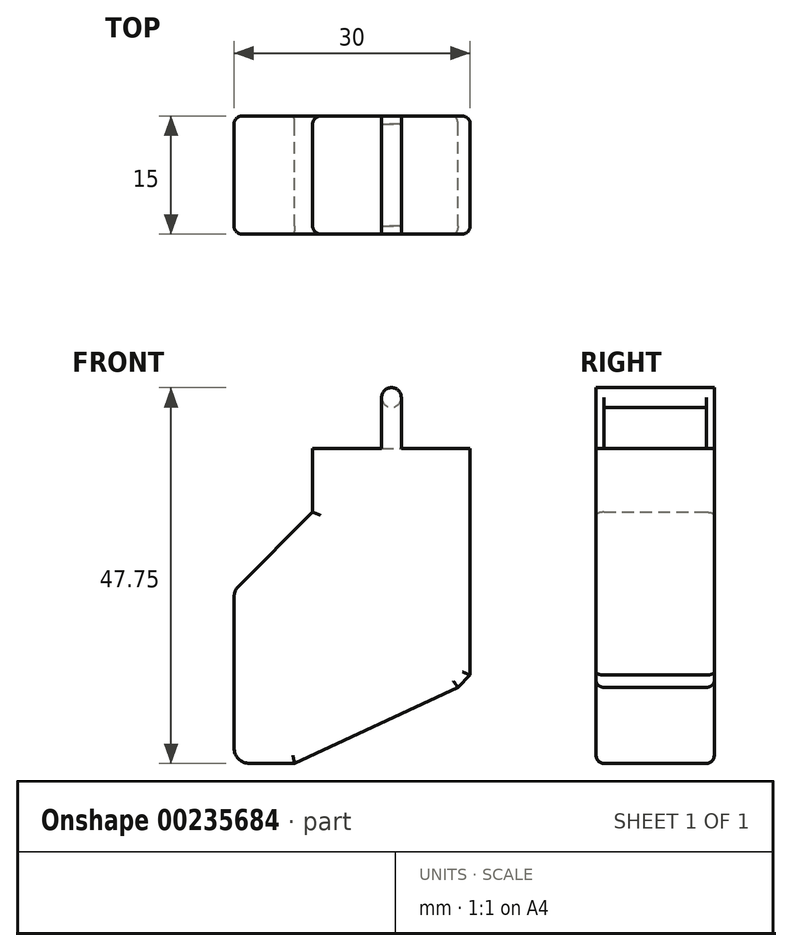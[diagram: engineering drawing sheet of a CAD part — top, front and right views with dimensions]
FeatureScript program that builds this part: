
annotation { "Feature Type Name" : "Feature", "Feature Type Description" : "" }
export const myFeature = defineFeature(function(context is Context, id is Id, definition is map)
    precondition{}
    {
        {
            var Q0;
            Q0=qCreatedBy(makeId("Front.planeOp"),FACE);
            var sketch = newSketch(context, id + "F0", { "sketchPlane" : qUnion([Q0])});
            skLineSegment(sketch, "E0", {"start": v(-8.09, 1.04) * mm, "end": v(-8.09, 15.54) * mm, "construction": true});
            skLineSegment(sketch, "E1", {"start": v(-8.09, 15.54) * mm, "end": v(-5.09, 15.54) * mm, "construction": true});
            skLineSegment(sketch, "E2", {"start": v(-5.09, 15.54) * mm, "end": v(-5.09, 1.04) * mm, "construction": true});
            skLineSegment(sketch, "E3", {"start": v(-5.09, 1.04) * mm, "end": v(-8.09, 1.04) * mm, "construction": true});
            skSolve(sketch);
        }
        {
            var Q0;
            Q0=qCreatedBy(makeId("Front.planeOp"),FACE);
            var sketch = newSketch(context, id + "F1", { "sketchPlane" : qUnion([Q0])});
            skPoint(sketch, "E4.1.end.orphan", {"position": v(-5.09, 15.54) * mm});
            skPoint(sketch, "E4.1.start.orphan", {"position": v(-8.09, 15.54) * mm});
            skPoint(sketch, "E5.end.orphan", {"position": v(-5.09, 1.04) * mm});
            skLineSegment(sketch, "E6", {"start": v(0, 12.27) * mm, "end": v(0, -9.67) * mm});
            skLineSegment(sketch, "E7", {"start": v(0, -9.67) * mm, "end": v(7.7, -9.67) * mm});
            skLineSegment(sketch, "E8", {"start": v(30, 1.56) * mm, "end": v(28.44, 0) * mm});
            skLineSegment(sketch, "E9", {"start": v(28.44, 0) * mm, "end": v(7.7, -9.67) * mm});
            skLineSegment(sketch, "E10", {"start": v(30, 1.56) * mm, "end": v(30, 30.33) * mm});
            skLineSegment(sketch, "E11", {"start": v(30, 30.33) * mm, "end": v(10, 30.33) * mm});
            skLineSegment(sketch, "E12", {"start": v(10, 30.33) * mm, "end": v(10, 22.27) * mm});
            skLineSegment(sketch, "E13", {"start": v(0, 12.27) * mm, "end": v(10, 22.27) * mm});
            skSolve(sketch);
        }
        {
            var Q0;
            Q0 = qSketchRegion(id + "F1", true);
            extrude(context, id + "F2", {"entities" : qUnion([Q0]), "depth" : 15 * mm});
        }
        {
            var Q0;
            Q0=makeQuery(id+"F2.opExtrude","SWEPT_EDGE",EDGE,{"disambiguationData":[OSD([sQuery(id+"F1.wireOp",EDGE,"lijkwqT2-R6P2-cXsj-bacL-RCKowQKFpfPk"),sQuery(id+"F1.wireOp",EDGE,"E6")])]});
            fillet(context, id + "F3", {"entities" : qUnion([Q0]), "radius" : 2 * mm, "tangentPropagation" : true, "allowEdgeOverflow" : false});
        }
        {
            var Q0;
            Q0=makeQuery(id+"F2.opExtrude","CAP_EDGE",EDGE,{"disambiguationData":[OSD([sQuery(id+"F1.wireOp",EDGE,"E13")])],"isStart":false});
            var Q1;
            Q1=makeQuery(id+"F2.opExtrude","CAP_EDGE",EDGE,{"disambiguationData":[OSD([sQuery(id+"F1.wireOp",EDGE,"E12")])],"isStart":false});
            var Q2;
            Q2=makeQuery(id+"F2.opExtrude","CAP_EDGE",EDGE,{"disambiguationData":[OSD([sQuery(id+"F1.wireOp",EDGE,"E12")])],"isStart":true});
            var Q3;
            Q3=makeQuery(id+"F2.opExtrude","CAP_EDGE",EDGE,{"disambiguationData":[OSD([sQuery(id+"F1.wireOp",EDGE,"E13")])],"isStart":true});
            var Q4;
            Q4=makeQuery(id+"F2.opExtrude","CAP_EDGE",EDGE,{"disambiguationData":[OSD([sQuery(id+"F1.wireOp",EDGE,"E9")])],"isStart":false});
            var Q5;
            Q5=makeQuery(id+"F2.opExtrude","CAP_EDGE",EDGE,{"disambiguationData":[OSD([sQuery(id+"F1.wireOp",EDGE,"E10")])],"isStart":false});
            var Q6;
            Q6=makeQuery(id+"F2.opExtrude","CAP_EDGE",EDGE,{"disambiguationData":[OSD([sQuery(id+"F1.wireOp",EDGE,"E8")])],"isStart":false});
            var Q7;
            Q7=makeQuery(id+"F2.opExtrude","CAP_EDGE",EDGE,{"disambiguationData":[OSD([sQuery(id+"F1.wireOp",EDGE,"E8")])],"isStart":true});
            var Q8;
            Q8=makeQuery(id+"F2.opExtrude","CAP_EDGE",EDGE,{"disambiguationData":[OSD([sQuery(id+"F1.wireOp",EDGE,"E10")])],"isStart":true});
            var Q9;
            Q9=makeQuery(id+"F2.opExtrude","CAP_EDGE",EDGE,{"disambiguationData":[OSD([sQuery(id+"F1.wireOp",EDGE,"E9")])],"isStart":true});
            fillet(context, id + "F4", {"entities" : qUnion([Q0, Q1, Q2, Q3, Q4, Q5, Q6, Q7, Q8, Q9]), "radius" : 1 * mm, "tangentPropagation" : true, "allowEdgeOverflow" : false});
        }
        {
            var Q0;
            Q0=makeQuery(id+"F2.opExtrude","CAP_FACE",FACE,{"disambiguationData":[OSD([sQuery(id+"F1.wireOp",EDGE,"E6"),sQuery(id+"F1.wireOp",EDGE,"E7"),sQuery(id+"F1.wireOp",EDGE,"E8"),sQuery(id+"F1.wireOp",EDGE,"E9"),sQuery(id+"F1.wireOp",EDGE,"E10"),sQuery(id+"F1.wireOp",EDGE,"E11"),sQuery(id+"F1.wireOp",EDGE,"E12"),sQuery(id+"F1.wireOp",EDGE,"E13")])],"isStart":false});
            var sketch = newSketch(context, id + "F5", { "sketchPlane" : qUnion([Q0])});
            skLineSegment(sketch, "E14", {"start": v(28.44, 0) * mm, "end": v(10, 22.27) * mm});
            skLineSegment(sketch, "E15.0", {"start": v(10, 22.27) * mm, "end": v(10, 30.33) * mm, "construction": true});
            skLineSegment(sketch, "E16.0", {"start": v(28.44, 0) * mm, "end": v(7.7, -9.67) * mm, "construction": true});
            skSolve(sketch);
        }
        {
            var Q0;
            Q0=qCreatedBy(makeId("Front.planeOp"),FACE);
            var sketch = newSketch(context, id + "F6", { "sketchPlane" : qUnion([Q0])});
            skLineSegment(sketch, "E17.0", {"start": v(29, 30.33) * mm, "end": v(11, 30.33) * mm});
            skLineSegment(sketch, "E18.0", {"start": v(10, 30.33) * mm, "end": v(11, 30.33) * mm});
            skLineSegment(sketch, "E19.0", {"start": v(29, 30.33) * mm, "end": v(30, 30.33) * mm});
            skLineSegment(sketch, "E20", {"start": v(18.75, 30.33) * mm, "end": v(18.75, 36.83) * mm});
            skLineSegment(sketch, "E21", {"start": v(18.75, 36.83) * mm, "end": v(21.25, 36.83) * mm, "construction": true});
            skLineSegment(sketch, "E22", {"start": v(21.25, 36.83) * mm, "end": v(21.25, 30.33) * mm});
            skArc(sketch, "E23", {"start": v(21.25, 36.83) * mm, "mid": v(20, 38.08) * mm, "end": v(18.75, 36.83) * mm});
            skSolve(sketch);
        }
        {
            var Q0;
            Q0 = qSketchRegion(id + "F6", true);
            extrude(context, id + "F7", {"entities" : qUnion([Q0]), "operationType" : NewBodyOperationType.ADD, "depth" : 15 * mm});
        }
        {
            var Q0;
            {var subQ0=sQuery(id+"F1.wireOp",EDGE,"E12");var subQ2=sQuery(id+"F1.wireOp",EDGE,"E11");Q0=makeQuery(id+"F7.boolean.opBoolean","SPLIT",FACE,{"disambiguationData":[TD([makeQuery(id+"F2.opExtrude","SWEPT_FACE",FACE,{"disambiguationData":[OSD([subQ0])]})])],"derivedFrom":makeQuery(id+"F2.opExtrude","SWEPT_FACE",FACE,{"disambiguationData":[OSD([subQ2])]})});}
            var sketch = newSketch(context, id + "F8", { "sketchPlane" : qUnion([Q0])});
            skLineSegment(sketch, "E24.bottom", {"start": v(18.3, -1) * mm, "end": v(22, -1) * mm});
            skLineSegment(sketch, "E24.top", {"start": v(18.3, -14) * mm, "end": v(22, -14) * mm});
            skLineSegment(sketch, "E24.left", {"start": v(18.3, -1) * mm, "end": v(18.3, -14) * mm});
            skLineSegment(sketch, "E24.right", {"start": v(22, -1) * mm, "end": v(22, -14) * mm});
            skSolve(sketch);
        }
        {
            var Q0;
            Q0 = qSketchRegion(id + "F8", true);
            extrude(context, id + "F9", {"entities" : qUnion([Q0]), "operationType" : NewBodyOperationType.REMOVE, "depth" : 25 * mm});
        }
        {
            var Q0;
            Q0=makeQuery(id+"F9.boolean.opBoolean","COPY",FACE,{"derivedFrom":makeQuery(id+"F9.opExtrude","SWEPT_FACE",FACE,{"disambiguationData":[OSD([sQuery(id+"F8.wireOp",EDGE,"E24.bottom")])]})});
            var sketch = newSketch(context, id + "F10", { "sketchPlane" : qUnion([Q0])});
            skCircle(sketch, "E25", {"center": v(20, 36.83) * mm, "radius": 1.25 * mm});
            skSolve(sketch);
        }
        {
            var Q0;
            Q0 = qSketchRegion(id + "F10", true);
            extrude(context, id + "F11", {"entities" : qUnion([Q0]), "operationType" : NewBodyOperationType.ADD, "depth" : 13 * mm});
        }
    });
